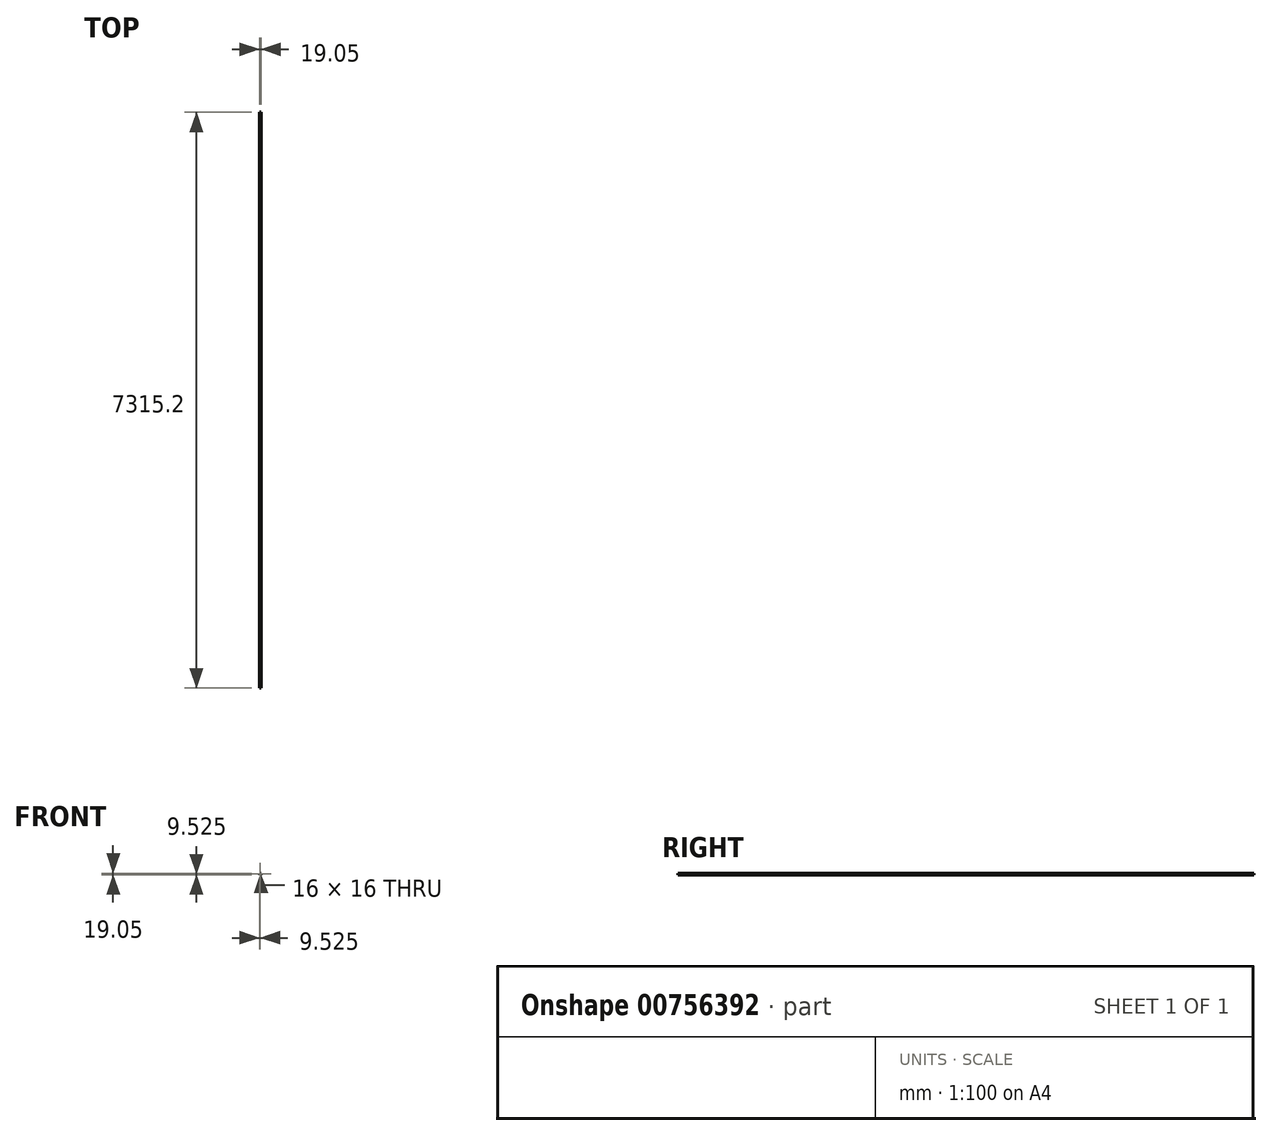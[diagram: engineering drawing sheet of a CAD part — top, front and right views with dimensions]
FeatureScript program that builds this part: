
annotation { "Feature Type Name" : "Feature", "Feature Type Description" : "" }
export const myFeature = defineFeature(function(context is Context, id is Id, definition is map)
    precondition{}
    {
        {
            var Q0;
            Q0=qCreatedBy(makeId("Front.planeOp"),FACE);
            var sketch = newSketch(context, id + "F0", { "sketchPlane" : qUnion([Q0])});
            skLineSegment(sketch, "E0.bottom", {"start": v(1.52, 17.53) * mm, "end": v(17.53, 17.53) * mm});
            skLineSegment(sketch, "E0.top", {"start": v(1.52, 1.52) * mm, "end": v(17.53, 1.52) * mm});
            skLineSegment(sketch, "E0.left", {"start": v(1.52, 17.53) * mm, "end": v(1.52, 1.52) * mm});
            skLineSegment(sketch, "E0.right", {"start": v(17.53, 17.53) * mm, "end": v(17.53, 1.52) * mm});
            skLineSegment(sketch, "E1.bottom", {"start": v(0, 0) * mm, "end": v(19.05, 0) * mm});
            skLineSegment(sketch, "E1.top", {"start": v(0, 19.05) * mm, "end": v(19.05, 19.05) * mm});
            skLineSegment(sketch, "E1.left", {"start": v(0, 0) * mm, "end": v(0, 19.05) * mm});
            skLineSegment(sketch, "E1.right", {"start": v(19.05, 0) * mm, "end": v(19.05, 19.05) * mm});
            skSolve(sketch);
        }
        {
            var Q0;
            Q0=makeQuery(id+"F0.imprint","IMPRINT",FACE,{"disambiguationData":[TD([[makeQuery(id+"F0.imprint","IMPRINT",EDGE,{"derivedFrom":sQuery(id+"F0.wireOp",EDGE,"E0.bottom")}),1.0]])]});
            extrude(context, id + "F1", {"entities" : qUnion([Q0]), "depth" : 7315.2 * mm, "offsetDistance" : 25.4 * mm});
        }
    });
